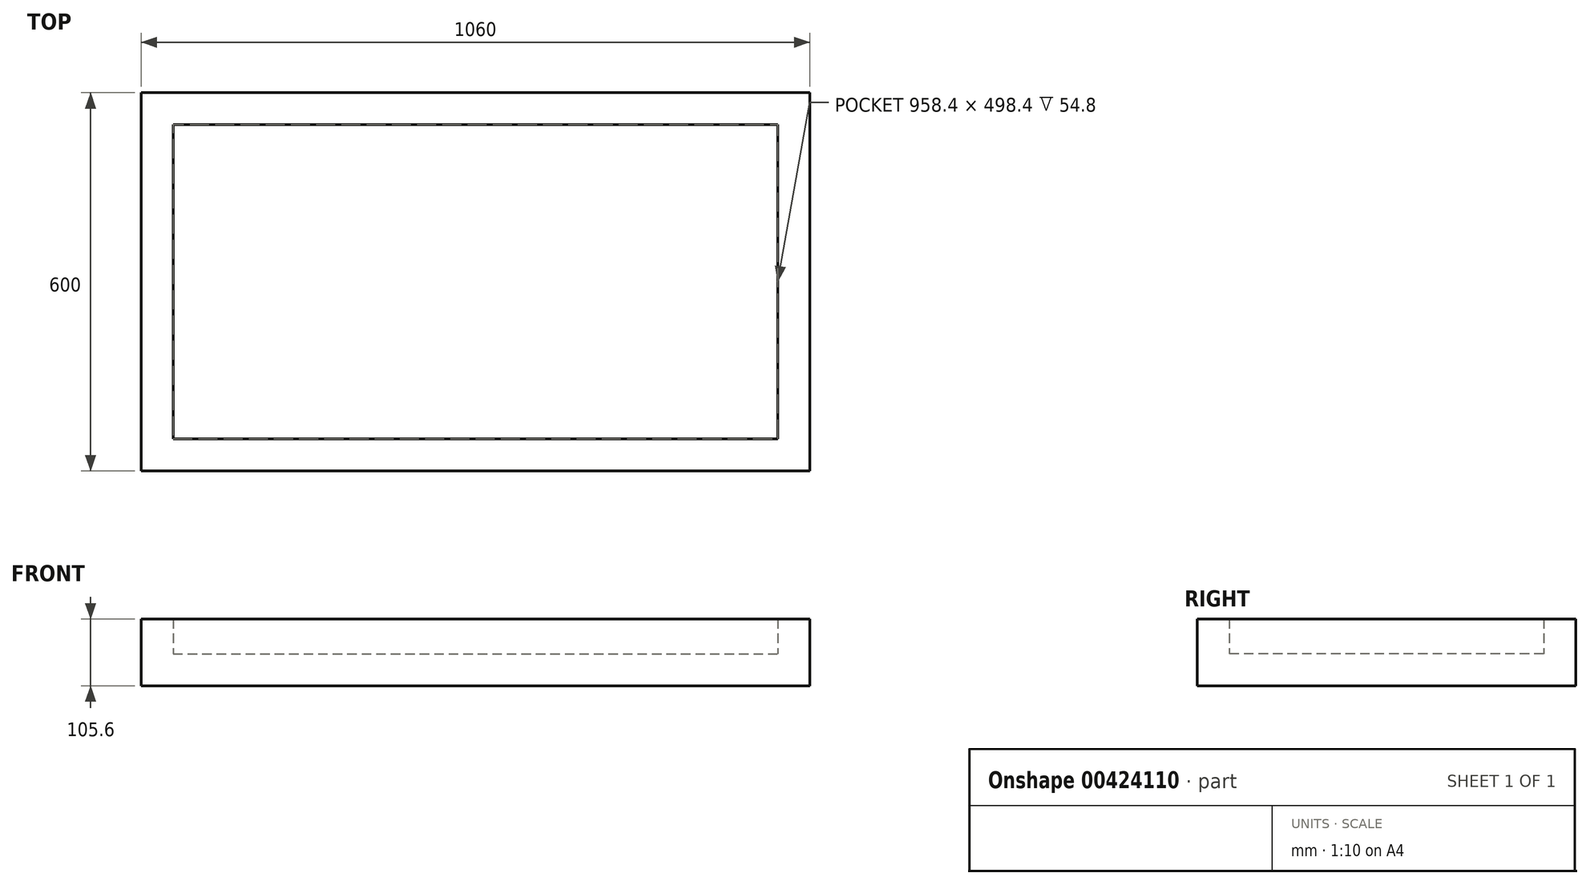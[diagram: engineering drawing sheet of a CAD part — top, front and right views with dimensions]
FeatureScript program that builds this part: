
annotation { "Feature Type Name" : "Feature", "Feature Type Description" : "" }
export const myFeature = defineFeature(function(context is Context, id is Id, definition is map)
    precondition{}
    {
        {
            var Q0;
            Q0=qCreatedBy(makeId("Top.planeOp"),FACE);
            var sketch = newSketch(context, id + "F0", { "sketchPlane" : qUnion([Q0])});
            skLineSegment(sketch, "E0.bottom", {"start": v(0, 0) * mm, "end": v(1060, 0) * mm});
            skLineSegment(sketch, "E0.top", {"start": v(0, -600) * mm, "end": v(1060, -600) * mm});
            skLineSegment(sketch, "E0.left", {"start": v(0, 0) * mm, "end": v(0, -600) * mm});
            skLineSegment(sketch, "E0.right", {"start": v(1060, 0) * mm, "end": v(1060, -600) * mm});
            skSolve(sketch);
        }
        {
            var Q0;
            Q0=makeQuery(id+"F0.imprint","IMPRINT",FACE,{"disambiguationData":[TD([[makeQuery(id+"F0.imprint","IMPRINT",EDGE,{"derivedFrom":sQuery(id+"F0.wireOp",EDGE,"E0.bottom")}),-1.0]])]});
            extrude(context, id + "F1", {"entities" : qUnion([Q0]), "depth" : 4 * mm});
        }
        {
            var Q0;
            Q0=makeQuery(id+"F1.opExtrude","CAP_FACE",FACE,{"disambiguationData":[OSD([sQuery(id+"F0.wireOp",EDGE,"E0.bottom"),sQuery(id+"F0.wireOp",EDGE,"E0.top"),sQuery(id+"F0.wireOp",EDGE,"E0.left"),sQuery(id+"F0.wireOp",EDGE,"E0.right")])],"isStart":false});
            var sketch = newSketch(context, id + "F2", { "sketchPlane" : qUnion([Q0])});
            skLineSegment(sketch, "E1.bottom", {"start": v(0, 0) * mm, "end": v(1060, 0) * mm});
            skLineSegment(sketch, "E1.top", {"start": v(0, -600) * mm, "end": v(1060, -600) * mm});
            skLineSegment(sketch, "E1.left", {"start": v(0, 0) * mm, "end": v(0, -600) * mm});
            skLineSegment(sketch, "E1.right", {"start": v(1060, 0) * mm, "end": v(1060, -600) * mm});
            skSolve(sketch);
        }
        {
            var Q0;
            Q0 = qSketchRegion(id + "F2", true);
            extrude(context, id + "F3", {"entities" : qUnion([Q0]), "operationType" : NewBodyOperationType.ADD, "depth" : 101.6 * mm});
        }
        {
            var Q0;
            Q0=makeQuery(id+"F3.opExtrude","CAP_FACE",FACE,{"disambiguationData":[OSD([sQuery(id+"F2.wireOp",EDGE,"E1.bottom"),sQuery(id+"F2.wireOp",EDGE,"E1.top"),sQuery(id+"F2.wireOp",EDGE,"E1.left"),sQuery(id+"F2.wireOp",EDGE,"E1.right")])],"isStart":false});
            shell(context, id + "F4", {"entities" : qUnion([Q0]), "thickness" : 50.8 * mm});
        }
    });
